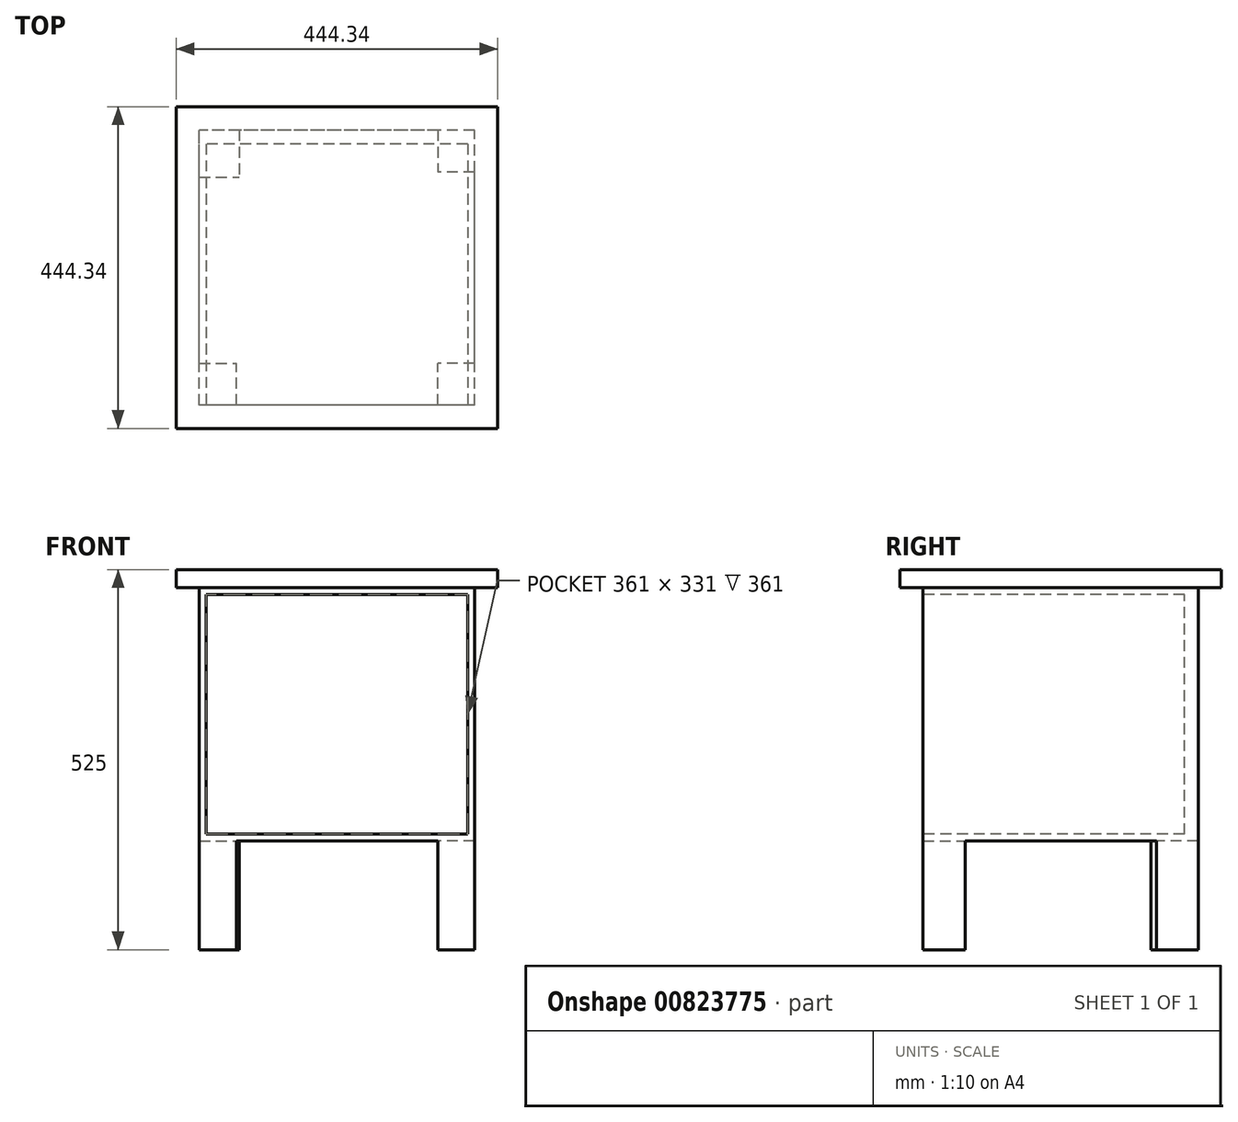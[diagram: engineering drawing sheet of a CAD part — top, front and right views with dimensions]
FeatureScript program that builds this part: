
annotation { "Feature Type Name" : "Feature", "Feature Type Description" : "" }
export const myFeature = defineFeature(function(context is Context, id is Id, definition is map)
    precondition{}
    {
        {
            var Q0;
            Q0=qCreatedBy(makeId("Top.planeOp"),FACE);
            var sketch = newSketch(context, id + "F0", { "sketchPlane" : qUnion([Q0])});
            skLineSegment(sketch, "E0.bottom", {"start": v(190, -190) * mm, "end": v(-190, -190) * mm});
            skLineSegment(sketch, "E0.top", {"start": v(190, 190) * mm, "end": v(-190, 190) * mm});
            skLineSegment(sketch, "E0.left", {"start": v(190, -190) * mm, "end": v(190, 190) * mm});
            skLineSegment(sketch, "E0.right", {"start": v(-190, -190) * mm, "end": v(-190, 190) * mm});
            skPoint(sketch, "E0.middle", {"position": v(0, 0) * mm});
            skSolve(sketch);
        }
        {
            var Q0;
            Q0=makeQuery(id+"F0.imprint","IMPRINT",FACE,{"disambiguationData":[TD([[makeQuery(id+"F0.imprint","IMPRINT",EDGE,{"derivedFrom":sQuery(id+"F0.wireOp",EDGE,"E0.bottom")}),-1.0]])]});
            extrude(context, id + "F1", {"entities" : qUnion([Q0]), "depth" : 350 * mm, "offsetDistance" : 25 * mm});
        }
        {
            var Q0;
            Q0=makeQuery(id+"F1.opExtrude","SWEPT_FACE",FACE,{"disambiguationData":[OSD([sQuery(id+"F0.wireOp",EDGE,"E0.bottom")])]});
            var sketch = newSketch(context, id + "F2", { "sketchPlane" : qUnion([Q0])});
            skLineSegment(sketch, "E1.bottom", {"start": v(180.5, 9.5) * mm, "end": v(-180.5, 9.5) * mm});
            skLineSegment(sketch, "E1.top", {"start": v(180.5, 340.5) * mm, "end": v(-180.5, 340.5) * mm});
            skLineSegment(sketch, "E1.left", {"start": v(180.5, 9.5) * mm, "end": v(180.5, 340.5) * mm});
            skLineSegment(sketch, "E1.right", {"start": v(-180.5, 9.5) * mm, "end": v(-180.5, 340.5) * mm});
            skPoint(sketch, "E1.middle", {"position": v(0, 175) * mm});
            skPoint(sketch, "E1.middle.positionSnap0", {"position": v(190, 175) * mm});
            skPoint(sketch, "E1.centerSnap0", {"position": v(190, 175) * mm});
            skSolve(sketch);
        }
        {
            var Q0;
            Q0=makeQuery(id+"F2.imprint","IMPRINT",FACE,{"disambiguationData":[TD([[makeQuery(id+"F2.imprint","IMPRINT",EDGE,{"derivedFrom":sQuery(id+"F2.wireOp",EDGE,"E1.bottom")}),-1.0]])]});
            extrude(context, id + "F3", {"entities" : qUnion([Q0]), "operationType" : NewBodyOperationType.REMOVE, "oppositeDirection" : true, "depth" : 361 * mm, "offsetDistance" : 25 * mm});
        }
        {
            var Q0;
            Q0=makeQuery(id+"F1.opExtrude","CAP_FACE",FACE,{"disambiguationData":[OSD([sQuery(id+"F0.wireOp",EDGE,"E0.bottom"),sQuery(id+"F0.wireOp",EDGE,"E0.top"),sQuery(id+"F0.wireOp",EDGE,"E0.left"),sQuery(id+"F0.wireOp",EDGE,"E0.right")])],"isStart":true});
            var sketch = newSketch(context, id + "F4", { "sketchPlane" : qUnion([Q0])});
            skLineSegment(sketch, "E2.bottom", {"start": v(190, 190) * mm, "end": v(139.63, 190) * mm});
            skLineSegment(sketch, "E2.top", {"start": v(190, 131.88) * mm, "end": v(139.63, 131.88) * mm});
            skLineSegment(sketch, "E2.left", {"start": v(190, 190) * mm, "end": v(190, 131.88) * mm});
            skLineSegment(sketch, "E2.right", {"start": v(139.63, 190) * mm, "end": v(139.63, 131.88) * mm});
            skLineSegment(sketch, "E3.bottom", {"start": v(190, -190) * mm, "end": v(139.63, -190) * mm});
            skLineSegment(sketch, "E3.top", {"start": v(190, -132.07) * mm, "end": v(139.63, -132.07) * mm});
            skLineSegment(sketch, "E3.left", {"start": v(190, -190) * mm, "end": v(190, -132.07) * mm});
            skLineSegment(sketch, "E3.right", {"start": v(139.63, -190) * mm, "end": v(139.63, -132.07) * mm});
            skLineSegment(sketch, "E4.bottom", {"start": v(-190, -190) * mm, "end": v(-134.67, -190) * mm});
            skLineSegment(sketch, "E4.top", {"start": v(-190, -125.03) * mm, "end": v(-134.67, -125.03) * mm});
            skLineSegment(sketch, "E4.left", {"start": v(-190, -190) * mm, "end": v(-190, -125.03) * mm});
            skLineSegment(sketch, "E4.right", {"start": v(-134.67, -190) * mm, "end": v(-134.67, -125.03) * mm});
            skLineSegment(sketch, "E5.bottom", {"start": v(-190, 190) * mm, "end": v(-138.73, 190) * mm});
            skLineSegment(sketch, "E5.top", {"start": v(-190, 131.88) * mm, "end": v(-138.73, 131.88) * mm});
            skLineSegment(sketch, "E5.left", {"start": v(-190, 190) * mm, "end": v(-190, 131.88) * mm});
            skLineSegment(sketch, "E5.right", {"start": v(-138.73, 190) * mm, "end": v(-138.73, 131.88) * mm});
            skSolve(sketch);
        }
        {
            var Q0;
            Q0=makeQuery(id+"F4.imprint","IMPRINT",FACE,{"disambiguationData":[TD([[makeQuery(id+"F4.imprint","IMPRINT",EDGE,{"derivedFrom":sQuery(id+"F4.wireOp",EDGE,"E2.bottom")}),1.0]])]});
            var Q1;
            Q1=makeQuery(id+"F4.imprint","IMPRINT",FACE,{"disambiguationData":[TD([[makeQuery(id+"F4.imprint","IMPRINT",EDGE,{"derivedFrom":sQuery(id+"F4.wireOp",EDGE,"E3.bottom")}),-1.0]])]});
            var Q2;
            Q2=makeQuery(id+"F4.imprint","IMPRINT",FACE,{"disambiguationData":[TD([[makeQuery(id+"F4.imprint","IMPRINT",EDGE,{"derivedFrom":sQuery(id+"F4.wireOp",EDGE,"E4.bottom")}),-1.0]])]});
            var Q3;
            Q3=makeQuery(id+"F4.imprint","IMPRINT",FACE,{"disambiguationData":[TD([[makeQuery(id+"F4.imprint","IMPRINT",EDGE,{"derivedFrom":sQuery(id+"F4.wireOp",EDGE,"E5.bottom")}),1.0]])]});
            extrude(context, id + "F5", {"entities" : qUnion([Q0, Q1, Q2, Q3]), "operationType" : NewBodyOperationType.ADD, "depth" : 150 * mm, "offsetDistance" : 25 * mm});
        }
        {
            var Q0;
            Q0=makeQuery(id+"F1.opExtrude","CAP_FACE",FACE,{"disambiguationData":[OSD([sQuery(id+"F0.wireOp",EDGE,"E0.bottom"),sQuery(id+"F0.wireOp",EDGE,"E0.top"),sQuery(id+"F0.wireOp",EDGE,"E0.left"),sQuery(id+"F0.wireOp",EDGE,"E0.right")])],"isStart":false});
            var sketch = newSketch(context, id + "F6", { "sketchPlane" : qUnion([Q0])});
            skLineSegment(sketch, "E6.bottom", {"start": v(222.17, 222.17) * mm, "end": v(-222.17, 222.17) * mm});
            skLineSegment(sketch, "E6.top", {"start": v(222.17, -222.17) * mm, "end": v(-222.17, -222.17) * mm});
            skLineSegment(sketch, "E6.left", {"start": v(222.17, 222.17) * mm, "end": v(222.17, -222.17) * mm});
            skLineSegment(sketch, "E6.right", {"start": v(-222.17, 222.17) * mm, "end": v(-222.17, -222.17) * mm});
            skPoint(sketch, "E6.middle", {"position": v(0, 0) * mm});
            skSolve(sketch);
        }
        {
            var Q0;
            Q0=makeQuery(id+"F6.imprint","IMPRINT",FACE,{"disambiguationData":[TD([[makeQuery(id+"F6.imprint","IMPRINT",EDGE,{"derivedFrom":sQuery(id+"F6.wireOp",EDGE,"E6.bottom")}),1.0]])]});
            var Q1;
            Q1=makeQuery(id+"F6.imprint","IMPRINT",FACE,{"disambiguationData":[TD([[makeQuery(id+"F6.imprint","IMPRINT",EDGE,{"derivedFrom":makeQuery(id+"F1.opExtrude","CAP_EDGE",EDGE,{"disambiguationData":[OSD([sQuery(id+"F0.wireOp",EDGE,"E0.bottom")])],"isStart":false})}),-1.0]])]});
            extrude(context, id + "F7", {"entities" : qUnion([Q0, Q1]), "operationType" : NewBodyOperationType.ADD, "depth" : 25 * mm, "offsetDistance" : 25 * mm});
        }
    });
